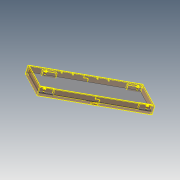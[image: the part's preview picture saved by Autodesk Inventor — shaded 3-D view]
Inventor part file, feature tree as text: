
AUTODESK INVENTOR PART (.ipt)
format: ipt  version: 2019 (Build 230136000, 136)  size: 318,976 bytes
history: native  units: mm
features: other x6, extrude x2, sketch x2, reference x2
ambient origin geometry x8: Origin, YZ Plane, XZ Plane, XY Plane, X Axis, Y Axis, Z Axis, Center Point
bodies: Solid1 (feature_tree)
feature tree (12):
  extrude  "Extrusion1"  Depth=10.0mm TaperAngle=0.0deg
  extrude  "Extrusion2"  [1 undecoded]
  sketch  "Sketch1"  dims[d0=2.0mm d1=0.0mm d2=10.0mm d3=0.0mm]
  reference  "Reference1"
  reference  "Reference2"
  sketch  "Sketch2"
  other  "Composite1"
  other  "Srf1"
  parser-record x1  (decoder bookkeeping rows leaked as tree rows — omitted from the tree; the rows remain in map.json)
  other  "Placca A.iam"
  other  "Case_A1:1"
  other  "Case_A2:1"
note: 1 required parameter value undecoded (feature->parameter linkage not recoverable at this tier; creation-order binding heuristic only, values carry confidence <= 0.55)
note: 1 file-system path scrubbed to <path> (originals preserved in map.json)
